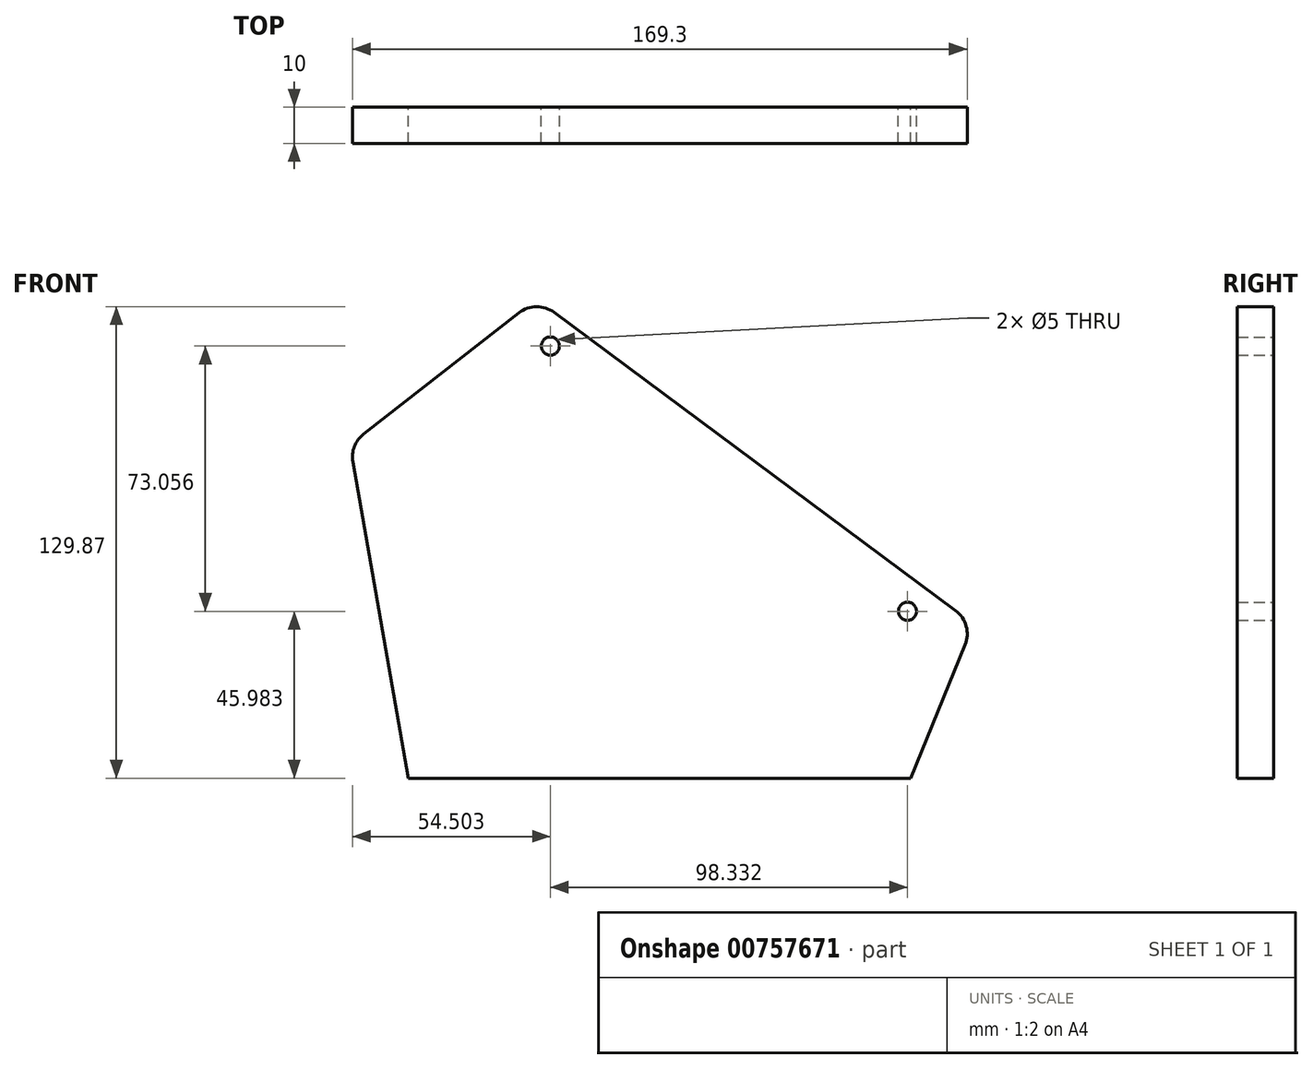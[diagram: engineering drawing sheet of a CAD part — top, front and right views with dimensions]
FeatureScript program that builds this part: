
annotation { "Feature Type Name" : "Feature", "Feature Type Description" : "" }
export const myFeature = defineFeature(function(context is Context, id is Id, definition is map)
    precondition{}
    {
        {
            var Q0;
            Q0=qCreatedBy(makeId("Front.planeOp"),FACE);
            var sketch = newSketch(context, id + "F0", { "sketchPlane" : qUnion([Q0])});
            skLineSegment(sketch, "E0", {"start": v(-50.1, 85.7) * mm, "end": v(-92.86, 52.33) * mm});
            skLineSegment(sketch, "E1", {"start": v(-80.53, -42.47) * mm, "end": v(-95.82, 44.64) * mm});
            skLineSegment(sketch, "E2", {"start": v(-80.53, -42.47) * mm, "end": v(57.77, -42.47) * mm});
            skLineSegment(sketch, "E3", {"start": v(57.77, -42.47) * mm, "end": v(72.77, -5.74) * mm});
            skLineSegment(sketch, "E4", {"start": v(70.13, 3.7) * mm, "end": v(-40.4, 85.82) * mm});
            skCircle(sketch, "E5", {"center": v(-41.44, 76.57) * mm, "radius": 2.5 * mm});
            skCircle(sketch, "E6", {"center": v(56.9, 3.51) * mm, "radius": 2.5 * mm});
            skLineSegment(sketch, "E7", {"start": v(-41.44, 76.57) * mm, "end": v(56.9, 3.51) * mm});
            skPoint(sketch, "E8.visualSharp", {"position": v(-45.3, 89.46) * mm});
            skArc(sketch, "E8.filletArc", {"start": v(-40.4, 85.82) * mm, "mid": v(-45.27, 87.4) * mm, "end": v(-50.1, 85.7) * mm});
            skPoint(sketch, "E9.visualSharp", {"position": v(75.11, 0) * mm});
            skArc(sketch, "E9.filletArc", {"start": v(72.77, -5.74) * mm, "mid": v(73.07, -0.57) * mm, "end": v(70.13, 3.7) * mm});
            skPoint(sketch, "E10.visualSharp", {"position": v(-96.65, 49.37) * mm});
            skArc(sketch, "E10.filletArc", {"start": v(-92.86, 52.33) * mm, "mid": v(-95.4, 48.9) * mm, "end": v(-95.82, 44.64) * mm});
            skSolve(sketch);
        }
        {
            var Q0;
            Q0=makeQuery(id+"F0.imprint","IMPRINT",FACE,{"disambiguationData":[TD([[makeQuery(id+"F0.imprint","IMPRINT",EDGE,{"derivedFrom":sQuery(id+"F0.wireOp",EDGE,"E0")}),1.0]])]});
            extrude(context, id + "F1", {"entities" : qUnion([Q0]), "depth" : 10 * mm, "offsetDistance" : 25 * mm});
        }
    });
